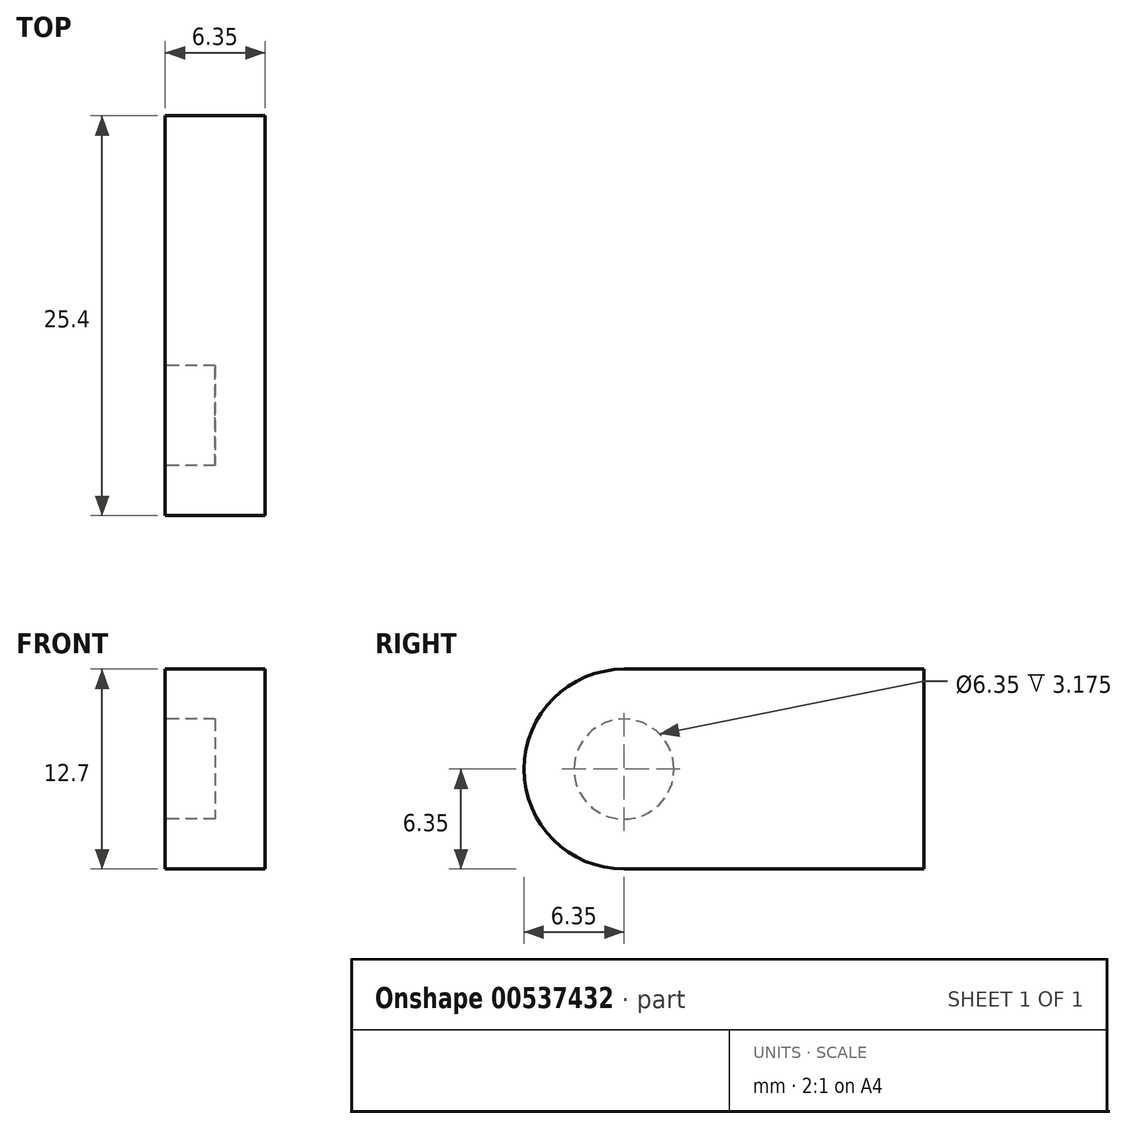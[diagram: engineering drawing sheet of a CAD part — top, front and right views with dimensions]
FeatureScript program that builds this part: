
annotation { "Feature Type Name" : "Feature", "Feature Type Description" : "" }
export const myFeature = defineFeature(function(context is Context, id is Id, definition is map)
    precondition{}
    {
        {
            var Q0;
            Q0=qCreatedBy(makeId("Front.planeOp"),FACE);
            var sketch = newSketch(context, id + "F0", { "sketchPlane" : qUnion([Q0])});
            skLineSegment(sketch, "E0.bottom", {"start": v(3.17, 6.35) * mm, "end": v(-3.18, 6.35) * mm});
            skLineSegment(sketch, "E0.top", {"start": v(3.17, -6.35) * mm, "end": v(-3.17, -6.35) * mm});
            skLineSegment(sketch, "E0.left", {"start": v(3.17, 6.35) * mm, "end": v(3.18, -6.35) * mm});
            skLineSegment(sketch, "E0.right", {"start": v(-3.18, 6.35) * mm, "end": v(-3.17, -6.35) * mm});
            skPoint(sketch, "E0.middle", {"position": v(0, 0) * mm});
            skSolve(sketch);
        }
        {
            var Q0;
            Q0 = qSketchRegion(id + "F0", true);
            extrude(context, id + "F1", {"entities" : qUnion([Q0]), "depth" : 25.4 * mm, "offsetDistance" : 25.4 * mm});
        }
        {
            var Q0;
            Q0=makeQuery(id+"F1.opExtrude","CAP_EDGE",EDGE,{"disambiguationData":[OSD([sQuery(id+"F0.wireOp",EDGE,"E0.bottom")])],"isStart":false});
            var Q1;
            Q1=makeQuery(id+"F1.opExtrude","CAP_EDGE",EDGE,{"disambiguationData":[OSD([sQuery(id+"F0.wireOp",EDGE,"E0.top")])],"isStart":false});
            fillet(context, id + "F2", {"entities" : qUnion([Q0, Q1]), "radius" : 6.35 * mm, "tangentPropagation" : true, "allowEdgeOverflow" : false});
        }
        {
            var Q0;
            Q0=makeQuery(id+"F1.opExtrude","SWEPT_FACE",FACE,{"disambiguationData":[OSD([sQuery(id+"F0.wireOp",EDGE,"E0.right")])]});
            var sketch = newSketch(context, id + "F3", { "sketchPlane" : qUnion([Q0])});
            skLineSegment(sketch, "E1", {"start": v(25.4, 0) * mm, "end": v(19.05, 0) * mm});
            skCircle(sketch, "E2", {"center": v(19.05, 0) * mm, "radius": 3.18 * mm});
            skSolve(sketch);
        }
        {
            var Q0;
            Q0=makeQuery(id+"F3.imprint","IMPRINT",FACE,{"disambiguationData":[TD([[makeQuery(id+"F3.imprint","IMPRINT",EDGE,{"derivedFrom":sQuery(id+"F3.wireOp",EDGE,"E2")}),1.0]])]});
            extrude(context, id + "F4", {"entities" : qUnion([Q0]), "operationType" : NewBodyOperationType.REMOVE, "oppositeDirection" : true, "depth" : 3.17 * mm, "offsetDistance" : 25.4 * mm});
        }
    });
